FCSTD DOCUMENT  (FreeCAD 0.20R29603 (Git))
Label: arcs
License: All rights reserved
LicenseURL: http://en.wikipedia.org/wiki/All_rights_reserved
objects: Part::FeaturePython×3, Part::Helix×2, Sketcher::SketchObject×1, Part::Part2DObjectPython×1, PartDesign::ShapeBinder×1, PartDesign::Plane×1, PartDesign::Body×1
note: 10 computed .brp shape members not serialized (recipe doc carries the construction recipe); baked Part::Feature solids carry a one-line shape summary decoded from their .brp

FEATURE [Sketcher::SketchObject] Sketch
  FullyConstrained = true
  MapMode = 5
  Support = -> [XY_Plane]
  sketch-geometry (15):
    g0: GeomPoint X=50 Y=40 Z=0
    g1: GeomPoint X=80 Y=75 Z=0
    g2: Circle CenterX=80 CenterY=75 CenterZ=0 NormalX=0 NormalY=0 NormalZ=1 AngleXU=0 Radius=46.0977
    g3: LineSegment StartX=50 StartY=40 StartZ=0 EndX=80 EndY=40 EndZ=0
    g4: LineSegment StartX=80 StartY=75 StartZ=0 EndX=80 EndY=40 EndZ=0
    g5: LineSegment StartX=50 StartY=40 StartZ=0 EndX=45 EndY=40 EndZ=0
    g6: Circle CenterX=80 CenterY=75 CenterZ=0 NormalX=0 NormalY=0 NormalZ=1 AngleXU=0 Radius=49.4975
    g7: ArcOfCircle CenterX=84.7205 CenterY=35.2795 CenterZ=0 NormalX=0 NormalY=0 NormalZ=1 AngleXU=0 Radius=40 StartAngle=1.68908 EndAngle=3.0233
    g8: ArcOfCircle CenterX=74.4896 CenterY=45.5104 CenterZ=0 NormalX=0 NormalY=0 NormalZ=1 AngleXU=0 Radius=30 StartAngle=3.32632 EndAngle=7.66925
    g9: ArcOfCircle CenterX=-1.33507 CenterY=46.8145 CenterZ=0 NormalX=0 NormalY=0 NormalZ=1 AngleXU=0 Radius=46.8335 StartAngle=4.7409 EndAngle=6.13716
    g10: LineSegment StartX=45 StartY=40 StartZ=0 EndX=-1.33507 EndY=46.8145 EndZ=0
    g11: LineSegment StartX=-1.33507 StartY=46.8145 StartZ=0 EndX=-1.07e-14 EndY=-7.1e-15 EndZ=0
    g12: ArcOfCircle CenterX=-20 CenterY=50 CenterZ=0 NormalX=0 NormalY=0 NormalZ=1 AngleXU=0 Radius=53.8516 StartAngle=4.3075 EndAngle=5.0929
    g13: LineSegment StartX=-20 StartY=50 StartZ=0 EndX=-1.07e-14 EndY=-7.1e-15 EndZ=0
    g14: LineSegment StartX=-20 StartY=50 StartZ=0 EndX=-41.2132 EndY=0.502525 EndZ=0
  constraints (37):
    c: Coincident(g2,g1)
    c: PointOnObject(g0,g2)
    c: Coincident(g3,g0)
    c: Horizontal(g3)
    c: Coincident(g4,g2)
    c: Coincident(g4,g3)
    c: Vertical(g4)
    c: Distance(g3) = 30
    c: Distance(g4) = 35
    c: DistanceX(g-2,g0) = 50
    c: DistanceY(g-1,g0) = 40
    c: Coincident(g5,g0)
    c: Horizontal(g5)
    c: Distance(g5) = 5
    c: Coincident(g6,g2)
    c: PointOnObject(g5,g6)
    c: Coincident(g7,g5)
    c: Coincident(g7,g2)
    c: Radius(g7) = 40
    c: Coincident(g8,g2)
    c: Coincident(g8,g5)
    c: Radius(g8) = 30
    c: Coincident(g9,g5)
    c: Coincident(g9,g-1)
    c: Coincident(g10,g5)
    c: Coincident(g10,g9)
    c: Coincident(g11,g9)
    c: Coincident(g11,g9)
    c: Angle(g11,g10) = 1.39626
    c: Coincident(g12,g9)
    c: Coincident(g13,g12)
    c: Coincident(g13,g9)
    c: Coincident(g14,g12)
    c: Coincident(g14,g12)
    c: Angle(g14,g13) = 0.785398
    c: DistanceY(g-1,g12) = 50
    c: DistanceX(g-2,g12) = -20
FEATURE [Part::Helix] Helix001
  Angle = 1
  AttacherType = Attacher::AttachEngine3D
  Height = 30
  LocalCoord = 0
  Pitch = 10
  Placement = pos=(-50,-30,0) rot=(0,0,1;1.5708rad)
  Radius = 30
  SegmentLength = 0
  Style = 1
FEATURE [Part::Helix] Helix
  Angle = 0
  AttacherType = Attacher::AttachEngine3D
  Height = 50
  LocalCoord = 1
  Pitch = 100
  Placement = pos=(-150,0,0) rot=(0,0,1;0rad)
  Radius = 50
  SegmentLength = 0
  Style = 1
FEATURE [Part::FeaturePython] Point  # WARN: FeaturePython — macro-defined, semantics opaque (R4)
  Placement = pos=(-150,-50,25) rot=(0,0,1;0rad)
  X = -150
  Y = -50
  Z = 25
FEATURE [Part::FeaturePython] Point001  # WARN: FeaturePython — macro-defined, semantics opaque (R4)
  Placement = pos=(-100,0,0) rot=(0,0,1;0rad)
  X = -100
  Y = 0
  Z = 0
FEATURE [Part::FeaturePython] Point002  # WARN: FeaturePython — macro-defined, semantics opaque (R4)
  Placement = pos=(-200,0,50) rot=(0,0,1;0rad)
  X = -200
  Y = 0
  Z = 50
FEATURE [Part::Part2DObjectPython] Arc  # Draft 2D object (typed FeaturePython)
  Area = 0
  FirstAngle = 0
  LastAngle = 167.241
  MakeFace = false
  Placement = pos=(-150,6.25,25) rot=(0.971821,-0.054158,-0.229416;3.11602rad)
  Radius = 56.25
FEATURE [PartDesign::ShapeBinder] CopyArc
  Placement = pos=(-150,6.25,25) rot=(0.971821,-0.054158,-0.229416;3.11602rad)
  TraceSupport = false
FEATURE [PartDesign::Plane] DatumPlane
  AttachmentOffset = pos=(513,0,0) rot=(0,0,1;0rad)
  Length = 745.896
  MapMode = 11
  Placement = pos=(-200.982,-503.573,50.4912) rot=(-0.658561,0.736293,0.155465;3.48578rad)
  ResizeMode = 0
  Support = -> [CopyArc]
  Width = 359.258
FEATURE [PartDesign::Body] Body
  Group = -> [Sketch,DatumPlane,CopyArc]
  Origin = -> Origin
